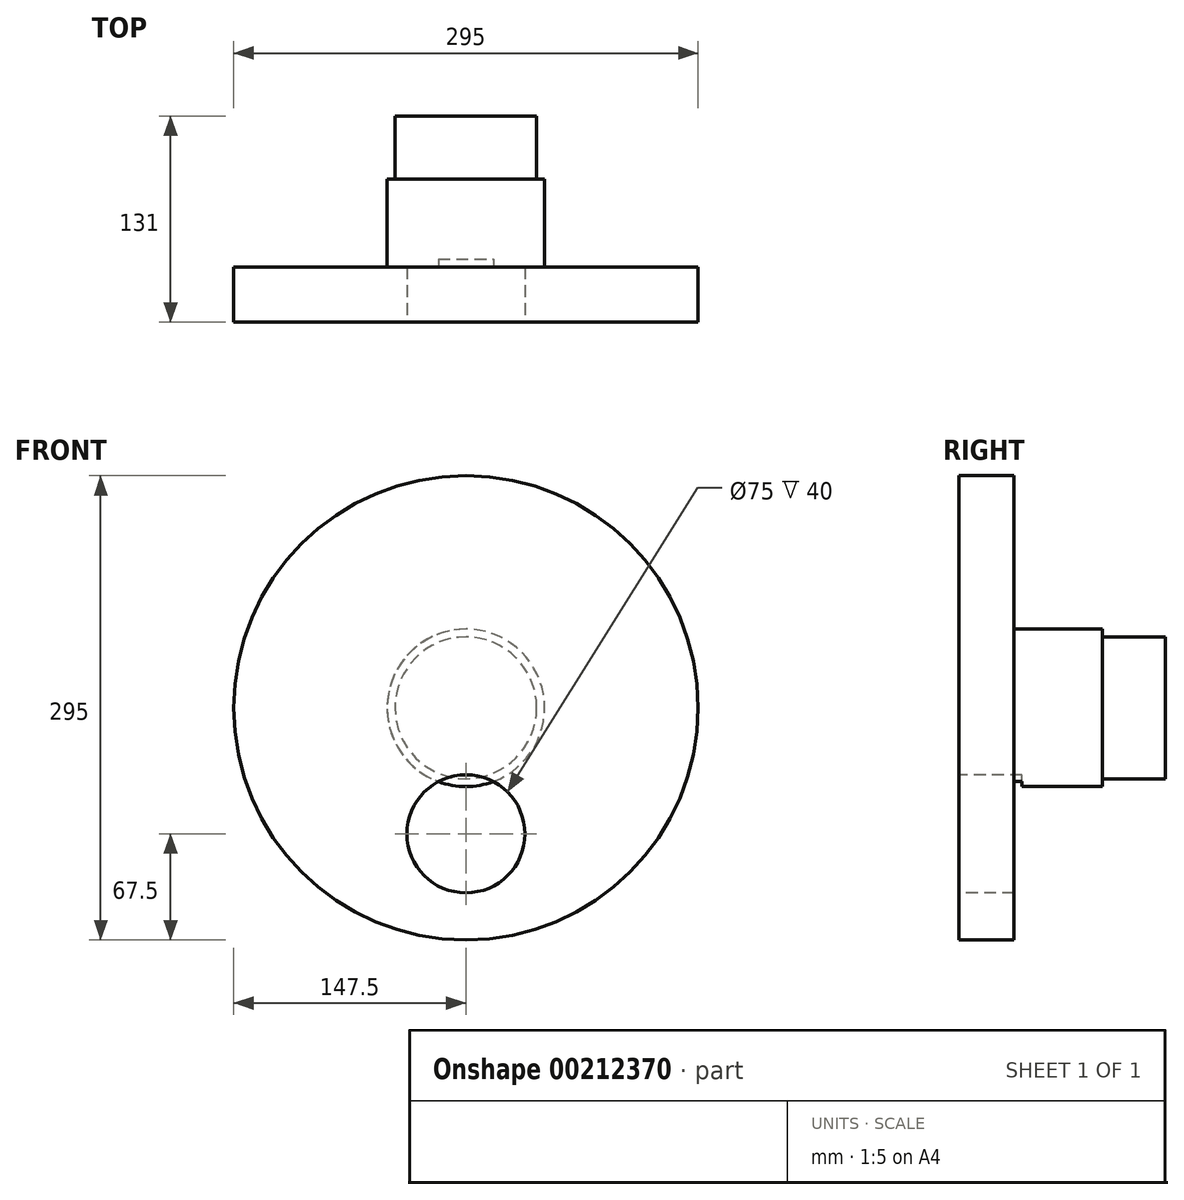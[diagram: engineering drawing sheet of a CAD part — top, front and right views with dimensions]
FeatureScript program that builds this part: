
annotation { "Feature Type Name" : "Feature", "Feature Type Description" : "" }
export const myFeature = defineFeature(function(context is Context, id is Id, definition is map)
    precondition{}
    {
        {
            var Q0;
            Q0=qCreatedBy(makeId("Front.planeOp"),FACE);
            var sketch = newSketch(context, id + "F0", { "sketchPlane" : qUnion([Q0])});
            skCircle(sketch, "E0", {"center": v(0, 0) * mm, "radius": 147.5 * mm});
            skSolve(sketch);
        }
        {
            var Q0;
            Q0=makeQuery(id+"F0.imprint","IMPRINT",FACE,{"disambiguationData":[TD([[makeQuery(id+"F0.imprint","IMPRINT",EDGE,{"derivedFrom":sQuery(id+"F0.wireOp",EDGE,"E0")}),1.0]])]});
            extrude(context, id + "F1", {"entities" : qUnion([Q0]), "depth" : 35 * mm});
        }
        {
            var Q0;
            Q0=makeQuery(id+"F1.opExtrude","CAP_FACE",FACE,{"disambiguationData":[OSD([sQuery(id+"F0.wireOp",EDGE,"E0")])],"isStart":true});
            var sketch = newSketch(context, id + "F2", { "sketchPlane" : qUnion([Q0])});
            skCircle(sketch, "E1", {"center": v(0, 0) * mm, "radius": 50 * mm});
            skSolve(sketch);
        }
        {
            var Q0;
            Q0=makeQuery(id+"F2.imprint","IMPRINT",FACE,{"disambiguationData":[TD([[makeQuery(id+"F2.imprint","IMPRINT",EDGE,{"derivedFrom":sQuery(id+"F2.wireOp",EDGE,"E1")}),1.0]])]});
            extrude(context, id + "F3", {"entities" : qUnion([Q0]), "operationType" : NewBodyOperationType.ADD, "depth" : 56 * mm});
        }
        {
            var Q0;
            Q0=makeQuery(id+"F3.opExtrude","CAP_FACE",FACE,{"disambiguationData":[OSD([sQuery(id+"F2.wireOp",EDGE,"E1")])],"isStart":false});
            var sketch = newSketch(context, id + "F4", { "sketchPlane" : qUnion([Q0])});
            skCircle(sketch, "E2", {"center": v(0, 0) * mm, "radius": 45 * mm});
            skSolve(sketch);
        }
        {
            var Q0;
            Q0=makeQuery(id+"F4.imprint","IMPRINT",FACE,{"disambiguationData":[TD([[makeQuery(id+"F4.imprint","IMPRINT",EDGE,{"derivedFrom":sQuery(id+"F4.wireOp",EDGE,"E2")}),1.0]])]});
            extrude(context, id + "F5", {"entities" : qUnion([Q0]), "operationType" : NewBodyOperationType.ADD, "depth" : 40 * mm});
        }
        {
            var Q0;
            Q0=makeQuery(id+"F1.opExtrude","CAP_FACE",FACE,{"disambiguationData":[OSD([sQuery(id+"F0.wireOp",EDGE,"E0")])],"isStart":false});
            var sketch = newSketch(context, id + "F6", { "sketchPlane" : qUnion([Q0])});
            skCircle(sketch, "E3", {"center": v(0, 0) * mm, "radius": 80 * mm});
            skCircle(sketch, "E4", {"center": v(0, -80) * mm, "radius": 37.5 * mm});
            skSolve(sketch);
        }
        {
            var Q0;
            {var subQ0=sQuery(id+"F6.wireOp",EDGE,"E4");var subQ1=sQuery(id+"F6.wireOp",EDGE,"E3");var subQ2=makeQuery(id+"F6.imprint","INTERSECT",VERTEX,{"disambiguationData":[OD(0.0)],"derivedFrom":[subQ1,subQ0]});Q0=makeQuery(id+"F6.imprint","IMPRINT",FACE,{"disambiguationData":[TD([[makeQuery(id+"F6.imprint","IMPRINT",EDGE,{"disambiguationData":[TD([[subQ2,-1.0]])],"derivedFrom":subQ1}),-1.0]])]});}
            var Q1;
            {var subQ0=sQuery(id+"F6.wireOp",EDGE,"E4");var subQ1=sQuery(id+"F6.wireOp",EDGE,"E3");var subQ2=makeQuery(id+"F6.imprint","INTERSECT",VERTEX,{"disambiguationData":[OD(0.0)],"derivedFrom":[subQ1,subQ0]});Q1=makeQuery(id+"F6.imprint","IMPRINT",FACE,{"disambiguationData":[TD([[makeQuery(id+"F6.imprint","IMPRINT",EDGE,{"disambiguationData":[TD([[subQ2,-1.0]])],"derivedFrom":subQ1}),1.0]])]});}
            extrude(context, id + "F7", {"entities" : qUnion([Q0, Q1]), "operationType" : NewBodyOperationType.REMOVE, "oppositeDirection" : true, "depth" : 40 * mm});
        }
    });
